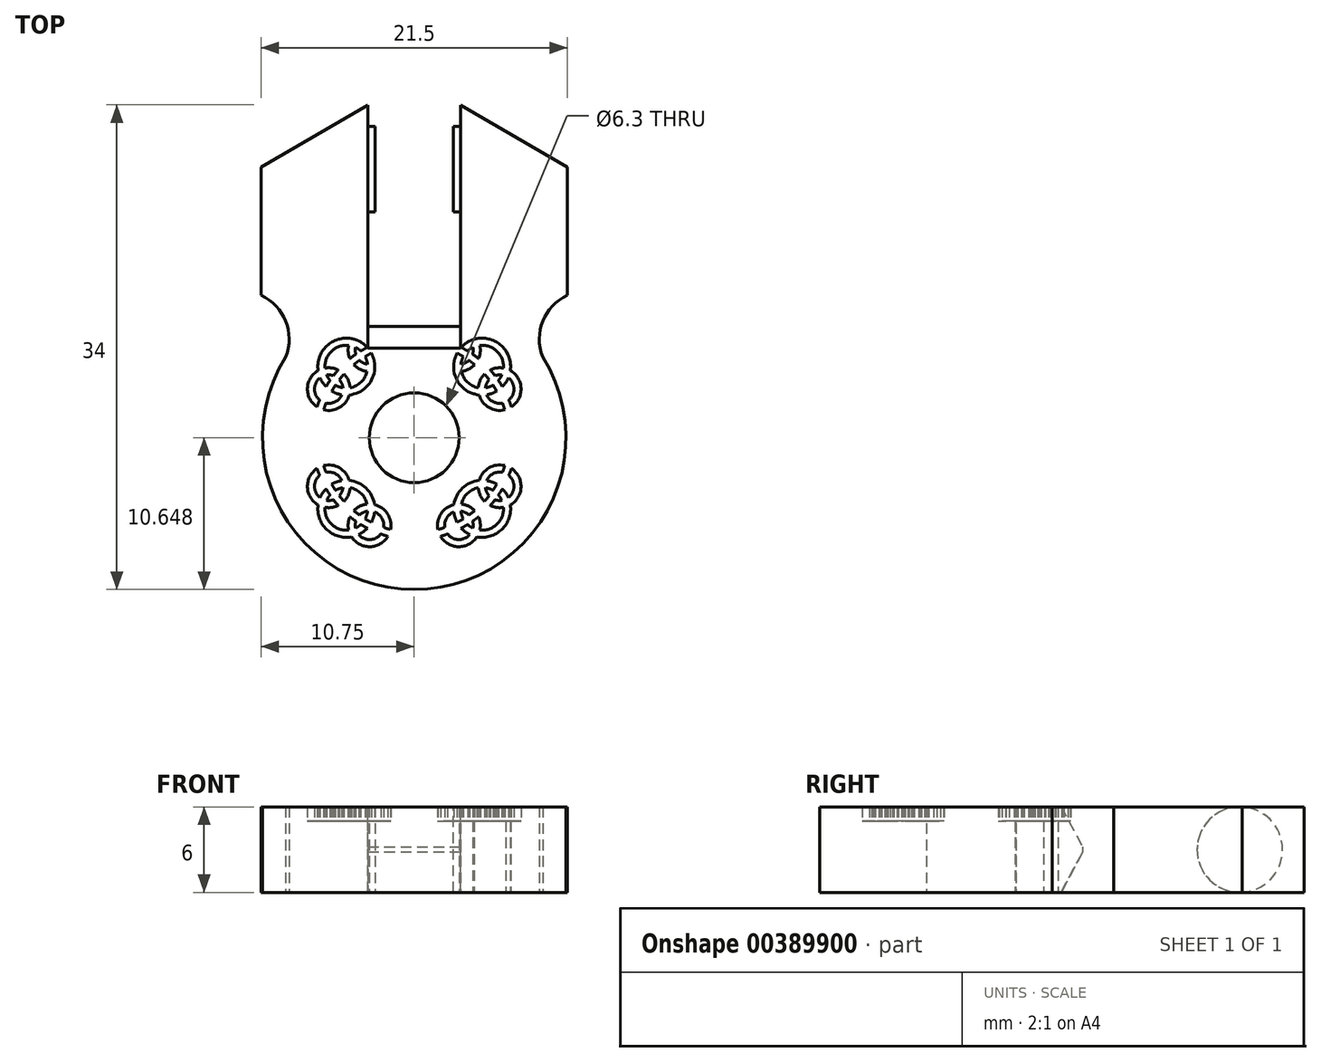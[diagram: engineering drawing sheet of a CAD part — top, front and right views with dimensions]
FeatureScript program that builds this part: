
annotation { "Feature Type Name" : "Feature", "Feature Type Description" : "" }
export const myFeature = defineFeature(function(context is Context, id is Id, definition is map)
    precondition{}
    {
        {
            var Q0;
            Q0=qCreatedBy(makeId("Top.planeOp"),FACE);
            var sketch = newSketch(context, id + "F0", { "sketchPlane" : qUnion([Q0])});
            skArc(sketch, "E0", {"start": v(29.04, 41) * mm, "mid": v(32.3, 20.22) * mm, "end": v(35.54, 41) * mm});
            skCircle(sketch, "E1", {"center": v(32.3, 30.87) * mm, "radius": 3.15 * mm});
            skLineSegment(sketch, "E2", {"start": v(35.54, 38.97) * mm, "end": v(35.54, 54.22) * mm});
            skLineSegment(sketch, "E3", {"start": v(43.04, 49.87) * mm, "end": v(35.54, 54.22) * mm});
            skLineSegment(sketch, "E4", {"start": v(43.04, 49.87) * mm, "end": v(43.04, 40.87) * mm});
            skLineSegment(sketch, "E5.MirrorCS", {"start": v(29.04, 38.97) * mm, "end": v(29.04, 54.22) * mm});
            skLineSegment(sketch, "E6.MirrorCS", {"start": v(21.54, 49.87) * mm, "end": v(29.04, 54.22) * mm});
            skLineSegment(sketch, "E7.MirrorCS", {"start": v(21.54, 49.87) * mm, "end": v(21.54, 40.87) * mm});
            skArc(sketch, "E8", {"start": v(43.04, 40.87) * mm, "mid": v(41.31, 39.04) * mm, "end": v(41.3, 36.53) * mm});
            skArc(sketch, "E9.MirrorCS", {"start": v(21.54, 40.87) * mm, "mid": v(23.27, 39.04) * mm, "end": v(23.27, 36.53) * mm});
            skArc(sketch, "E10", {"start": v(35.59, 24.52) * mm, "mid": v(35.87, 24.27) * mm, "end": v(36.2, 24.08) * mm});
            skArc(sketch, "E11", {"start": v(37.82, 27.17) * mm, "mid": v(37.57, 27.3) * mm, "end": v(37.3, 27.36) * mm});
            skArc(sketch, "E12", {"start": v(34.14, 23.96) * mm, "mid": v(35.4, 23.22) * mm, "end": v(36.7, 23.92) * mm});
            skArc(sketch, "E13", {"start": v(34.64, 24.11) * mm, "mid": v(35.4, 23.72) * mm, "end": v(36.2, 24.08) * mm});
            skArc(sketch, "E14", {"start": v(38.65, 28.91) * mm, "mid": v(37.54, 28.76) * mm, "end": v(36.85, 27.87) * mm});
            skArc(sketch, "E15", {"start": v(38.48, 28.44) * mm, "mid": v(37.82, 28.34) * mm, "end": v(37.37, 27.86) * mm});
            skArc(sketch, "E16.0", {"start": v(35.59, 24.52) * mm, "mid": v(35.82, 24.65) * mm, "end": v(36.04, 24.78) * mm});
            skArc(sketch, "E17.0", {"start": v(35.3, 24.94) * mm, "mid": v(35.52, 25.05) * mm, "end": v(35.73, 25.18) * mm});
            skArc(sketch, "E18.trimOffspring", {"start": v(34.14, 23.96) * mm, "mid": v(34.39, 24.03) * mm, "end": v(34.64, 24.11) * mm});
            skArc(sketch, "E19.trimOffspring", {"start": v(33.96, 24.43) * mm, "mid": v(34.2, 24.5) * mm, "end": v(34.44, 24.57) * mm});
            skArc(sketch, "E20.trimOffspring", {"start": v(38.08, 27.6) * mm, "mid": v(37.74, 27.76) * mm, "end": v(37.37, 27.86) * mm});
            skArc(sketch, "E21.trimOffspring", {"start": v(38.93, 28.22) * mm, "mid": v(39.03, 28.47) * mm, "end": v(39.1, 28.71) * mm});
            skArc(sketch, "E22.trimOffspring", {"start": v(38.48, 28.44) * mm, "mid": v(38.57, 28.68) * mm, "end": v(38.65, 28.91) * mm});
            skArc(sketch, "E23.trimOffspring", {"start": v(38.2, 26.85) * mm, "mid": v(38.35, 27.07) * mm, "end": v(38.48, 27.29) * mm});
            skArc(sketch, "E24.trimOffspring", {"start": v(37.82, 27.17) * mm, "mid": v(37.95, 27.38) * mm, "end": v(38.08, 27.6) * mm});
            skArc(sketch, "E25.trimOffspring", {"start": v(37.96, 26.51) * mm, "mid": v(38.2, 26.46) * mm, "end": v(38.44, 26.47) * mm});
            skArc(sketch, "E26.trimOffspring", {"start": v(37.63, 26.11) * mm, "mid": v(38.08, 25.97) * mm, "end": v(38.56, 25.98) * mm});
            skArc(sketch, "E27.trimOffspring", {"start": v(36.53, 25.74) * mm, "mid": v(36.1, 26.06) * mm, "end": v(35.6, 26.21) * mm});
            skArc(sketch, "E28.trimOffspring", {"start": v(36.13, 25.44) * mm, "mid": v(35.87, 25.62) * mm, "end": v(35.57, 25.71) * mm});
            skArc(sketch, "E29.trimOffspring", {"start": v(36.04, 24.78) * mm, "mid": v(36.22, 24.64) * mm, "end": v(36.4, 24.53) * mm});
            skArc(sketch, "E30.trimOffspring", {"start": v(37.63, 26.11) * mm, "mid": v(37.8, 26.3) * mm, "end": v(37.96, 26.51) * mm});
            skArc(sketch, "E31.trimOffspring", {"start": v(37.22, 26.4) * mm, "mid": v(37.39, 26.6) * mm, "end": v(37.54, 26.8) * mm});
            skArc(sketch, "E32.trimOffspring", {"start": v(36.13, 25.44) * mm, "mid": v(36.33, 25.59) * mm, "end": v(36.53, 25.74) * mm});
            skArc(sketch, "E33.trimOffspring", {"start": v(36.39, 25) * mm, "mid": v(36.6, 25.16) * mm, "end": v(36.8, 25.32) * mm});
            skArc(sketch, "E34.MirrorCS", {"start": v(37.63, 35.62) * mm, "mid": v(38.08, 35.76) * mm, "end": v(38.56, 35.75) * mm});
            skArc(sketch, "E35.MirrorCS", {"start": v(37.96, 35.22) * mm, "mid": v(38.2, 35.27) * mm, "end": v(38.44, 35.27) * mm});
            skArc(sketch, "E36.trimOffspring", {"start": v(39.04, 26.16) * mm, "mid": v(39.79, 27.42) * mm, "end": v(39.1, 28.71) * mm});
            skArc(sketch, "E37.trimOffspring", {"start": v(38.9, 26.67) * mm, "mid": v(39.29, 27.44) * mm, "end": v(38.93, 28.22) * mm});
            skArc(sketch, "E38.trimOffspring", {"start": v(38.44, 26.47) * mm, "mid": v(38.34, 26.67) * mm, "end": v(38.2, 26.85) * mm});
            skArc(sketch, "E39.trimOffspring", {"start": v(38.9, 26.67) * mm, "mid": v(38.72, 27) * mm, "end": v(38.48, 27.29) * mm});
            skArc(sketch, "E40.trimOffspring", {"start": v(36.8, 27.36) * mm, "mid": v(36.02, 26.97) * mm, "end": v(35.6, 26.21) * mm});
            skArc(sketch, "E41.trimOffspring", {"start": v(37.3, 27.36) * mm, "mid": v(37.37, 27.06) * mm, "end": v(37.54, 26.8) * mm});
            skArc(sketch, "E42.trimOffspring", {"start": v(36.8, 27.36) * mm, "mid": v(36.92, 26.84) * mm, "end": v(37.22, 26.4) * mm});
            skArc(sketch, "E43.trimOffspring", {"start": v(36.85, 27.87) * mm, "mid": v(35.68, 27.33) * mm, "end": v(35.08, 26.18) * mm});
            skArc(sketch, "E44.trimOffspring", {"start": v(35.57, 25.71) * mm, "mid": v(35.63, 25.44) * mm, "end": v(35.73, 25.18) * mm});
            skArc(sketch, "E45.trimOffspring", {"start": v(35.07, 25.66) * mm, "mid": v(35.15, 25.29) * mm, "end": v(35.3, 24.94) * mm});
            skArc(sketch, "E46.trimOffspring", {"start": v(35.07, 25.66) * mm, "mid": v(34.57, 25.23) * mm, "end": v(34.44, 24.57) * mm});
            skArc(sketch, "E47.trimOffspring", {"start": v(35.08, 26.18) * mm, "mid": v(34.17, 25.53) * mm, "end": v(33.96, 24.43) * mm});
            skArc(sketch, "E48.trimOffspring", {"start": v(36.4, 24.53) * mm, "mid": v(36.43, 24.77) * mm, "end": v(36.39, 25) * mm});
            skArc(sketch, "E49.trimOffspring", {"start": v(36.9, 24.4) * mm, "mid": v(36.92, 24.86) * mm, "end": v(36.8, 25.32) * mm});
            skArc(sketch, "E50.trimOffspring", {"start": v(36.9, 24.4) * mm, "mid": v(38.1, 24.8) * mm, "end": v(38.56, 25.98) * mm});
            skArc(sketch, "E51.trimOffspring", {"start": v(36.7, 23.92) * mm, "mid": v(38.44, 24.44) * mm, "end": v(39.04, 26.16) * mm});
            skArc(sketch, "E52.MirrorCS", {"start": v(38.48, 33.3) * mm, "mid": v(38.57, 33.06) * mm, "end": v(38.65, 32.82) * mm});
            skArc(sketch, "E53.MirrorCS", {"start": v(38.93, 33.51) * mm, "mid": v(39.03, 33.27) * mm, "end": v(39.1, 33.02) * mm});
            skArc(sketch, "E54.MirrorCS", {"start": v(38.9, 35.07) * mm, "mid": v(39.29, 34.3) * mm, "end": v(38.93, 33.51) * mm});
            skArc(sketch, "E55.MirrorCS", {"start": v(38.9, 35.07) * mm, "mid": v(38.72, 34.74) * mm, "end": v(38.48, 34.45) * mm});
            skArc(sketch, "E56.MirrorCS", {"start": v(38.2, 34.89) * mm, "mid": v(38.35, 34.67) * mm, "end": v(38.48, 34.45) * mm});
            skArc(sketch, "E57.MirrorCS", {"start": v(37.82, 34.56) * mm, "mid": v(37.95, 34.35) * mm, "end": v(38.08, 34.14) * mm});
            skArc(sketch, "E58.MirrorCS", {"start": v(36.85, 33.87) * mm, "mid": v(35.68, 34.4) * mm, "end": v(35.08, 35.55) * mm});
            skArc(sketch, "E59.MirrorCS", {"start": v(36.7, 37.82) * mm, "mid": v(38.44, 37.3) * mm, "end": v(39.04, 35.58) * mm});
            skArc(sketch, "E60.MirrorCS", {"start": v(36.9, 37.35) * mm, "mid": v(38.1, 36.94) * mm, "end": v(38.56, 35.75) * mm});
            skArc(sketch, "E61.MirrorCS", {"start": v(36.8, 34.38) * mm, "mid": v(36.02, 34.77) * mm, "end": v(35.6, 35.52) * mm});
            skArc(sketch, "E62.MirrorCS", {"start": v(39.04, 35.58) * mm, "mid": v(39.79, 34.32) * mm, "end": v(39.1, 33.02) * mm});
            skArc(sketch, "E63.MirrorCS", {"start": v(38.65, 32.82) * mm, "mid": v(37.54, 32.98) * mm, "end": v(36.85, 33.87) * mm});
            skArc(sketch, "E64.MirrorCS", {"start": v(38.48, 33.3) * mm, "mid": v(37.82, 33.4) * mm, "end": v(37.37, 33.88) * mm});
            skArc(sketch, "E65.MirrorCS", {"start": v(38.08, 34.14) * mm, "mid": v(37.74, 33.97) * mm, "end": v(37.37, 33.88) * mm});
            skArc(sketch, "E66.MirrorCS", {"start": v(37.82, 34.56) * mm, "mid": v(37.57, 34.44) * mm, "end": v(37.3, 34.37) * mm});
            skArc(sketch, "E67.MirrorCS", {"start": v(37.3, 34.37) * mm, "mid": v(37.37, 34.68) * mm, "end": v(37.54, 34.94) * mm});
            skArc(sketch, "E68.MirrorCS", {"start": v(36.8, 34.38) * mm, "mid": v(36.92, 34.9) * mm, "end": v(37.22, 35.33) * mm});
            skArc(sketch, "E69.MirrorCS", {"start": v(37.22, 35.33) * mm, "mid": v(37.39, 35.14) * mm, "end": v(37.54, 34.94) * mm});
            skArc(sketch, "E70.MirrorCS", {"start": v(37.63, 35.62) * mm, "mid": v(37.8, 35.43) * mm, "end": v(37.96, 35.22) * mm});
            skArc(sketch, "E71.MirrorCS", {"start": v(35.07, 36.08) * mm, "mid": v(35.15, 36.45) * mm, "end": v(35.3, 36.8) * mm});
            skArc(sketch, "E72.MirrorCS", {"start": v(35.59, 37.21) * mm, "mid": v(35.87, 37.46) * mm, "end": v(36.2, 37.66) * mm});
            skArc(sketch, "E73.MirrorCS", {"start": v(35.59, 37.21) * mm, "mid": v(35.82, 37.09) * mm, "end": v(36.04, 36.96) * mm});
            skArc(sketch, "E74.MirrorCS", {"start": v(35.3, 36.8) * mm, "mid": v(35.52, 36.68) * mm, "end": v(35.73, 36.56) * mm});
            skArc(sketch, "E75.MirrorCS", {"start": v(36.9, 37.35) * mm, "mid": v(36.92, 36.87) * mm, "end": v(36.8, 36.41) * mm});
            skArc(sketch, "E76.MirrorCS", {"start": v(36.53, 36) * mm, "mid": v(36.1, 35.67) * mm, "end": v(35.6, 35.52) * mm});
            skArc(sketch, "E77.MirrorCS", {"start": v(36.13, 36.3) * mm, "mid": v(35.87, 36.12) * mm, "end": v(35.57, 36.02) * mm});
            skArc(sketch, "E78.MirrorCS", {"start": v(36.39, 36.73) * mm, "mid": v(36.6, 36.57) * mm, "end": v(36.8, 36.41) * mm});
            skArc(sketch, "E79.MirrorCS", {"start": v(36.13, 36.3) * mm, "mid": v(36.33, 36.15) * mm, "end": v(36.53, 36) * mm});
            skArc(sketch, "E80.MirrorCS", {"start": v(38.44, 35.27) * mm, "mid": v(38.34, 35.07) * mm, "end": v(38.2, 34.89) * mm});
            skArc(sketch, "E81.MirrorCS", {"start": v(36.4, 37.2) * mm, "mid": v(36.43, 36.97) * mm, "end": v(36.39, 36.73) * mm});
            skArc(sketch, "E82.MirrorCS", {"start": v(36.04, 36.96) * mm, "mid": v(36.22, 37.1) * mm, "end": v(36.4, 37.2) * mm});
            skArc(sketch, "E83.MirrorCS", {"start": v(35.57, 36.02) * mm, "mid": v(35.63, 36.3) * mm, "end": v(35.73, 36.56) * mm});
            skArc(sketch, "E84.MirrorCS", {"start": v(25.54, 26.16) * mm, "mid": v(24.8, 27.42) * mm, "end": v(25.47, 28.71) * mm});
            skArc(sketch, "E85.MirrorCS", {"start": v(25.93, 28.91) * mm, "mid": v(27.04, 28.76) * mm, "end": v(27.73, 27.87) * mm});
            skArc(sketch, "E86.MirrorCS", {"start": v(25.65, 28.22) * mm, "mid": v(25.56, 28.47) * mm, "end": v(25.47, 28.71) * mm});
            skArc(sketch, "E87.MirrorCS", {"start": v(26.1, 28.44) * mm, "mid": v(26.01, 28.68) * mm, "end": v(25.93, 28.91) * mm});
            skArc(sketch, "E88.MirrorCS", {"start": v(26.1, 28.44) * mm, "mid": v(26.76, 28.34) * mm, "end": v(27.2, 27.86) * mm});
            skArc(sketch, "E89.MirrorCS", {"start": v(25.68, 26.67) * mm, "mid": v(25.3, 27.44) * mm, "end": v(25.65, 28.22) * mm});
            skArc(sketch, "E90.MirrorCS", {"start": v(27.89, 23.92) * mm, "mid": v(26.14, 24.44) * mm, "end": v(25.54, 26.16) * mm});
            skArc(sketch, "E91.MirrorCS", {"start": v(27.69, 24.4) * mm, "mid": v(26.48, 24.8) * mm, "end": v(26.02, 25.98) * mm});
            skArc(sketch, "E92.MirrorCS", {"start": v(25.68, 26.67) * mm, "mid": v(25.86, 27) * mm, "end": v(26.1, 27.29) * mm});
            skArc(sketch, "E93.MirrorCS", {"start": v(26.76, 27.17) * mm, "mid": v(27.01, 27.3) * mm, "end": v(27.29, 27.36) * mm});
            skArc(sketch, "E94.MirrorCS", {"start": v(26.5, 27.6) * mm, "mid": v(26.84, 27.76) * mm, "end": v(27.2, 27.86) * mm});
            skArc(sketch, "E95.MirrorCS", {"start": v(26.76, 27.17) * mm, "mid": v(26.63, 27.38) * mm, "end": v(26.5, 27.6) * mm});
            skArc(sketch, "E96.MirrorCS", {"start": v(28.05, 25.74) * mm, "mid": v(28.48, 26.06) * mm, "end": v(28.98, 26.21) * mm});
            skArc(sketch, "E97.MirrorCS", {"start": v(28.45, 25.44) * mm, "mid": v(28.7, 25.62) * mm, "end": v(29.01, 25.71) * mm});
            skArc(sketch, "E98.MirrorCS", {"start": v(29.01, 25.71) * mm, "mid": v(28.95, 25.44) * mm, "end": v(28.85, 25.18) * mm});
            skArc(sketch, "E99.MirrorCS", {"start": v(29.5, 25.66) * mm, "mid": v(29.43, 25.29) * mm, "end": v(29.28, 24.94) * mm});
            skArc(sketch, "E100.MirrorCS", {"start": v(29.5, 25.66) * mm, "mid": v(30.02, 25.23) * mm, "end": v(30.14, 24.57) * mm});
            skArc(sketch, "E101.MirrorCS", {"start": v(29.5, 26.18) * mm, "mid": v(30.41, 25.53) * mm, "end": v(30.62, 24.43) * mm});
            skArc(sketch, "E102.MirrorCS", {"start": v(30.62, 24.43) * mm, "mid": v(30.38, 24.5) * mm, "end": v(30.14, 24.57) * mm});
            skArc(sketch, "E103.MirrorCS", {"start": v(30.44, 23.96) * mm, "mid": v(30.2, 24.03) * mm, "end": v(29.94, 24.11) * mm});
            skArc(sketch, "E104.MirrorCS", {"start": v(30.44, 23.96) * mm, "mid": v(29.18, 23.22) * mm, "end": v(27.89, 23.92) * mm});
            skArc(sketch, "E105.MirrorCS", {"start": v(29.94, 24.11) * mm, "mid": v(29.17, 23.72) * mm, "end": v(28.39, 24.08) * mm});
            skArc(sketch, "E106.MirrorCS", {"start": v(29, 24.52) * mm, "mid": v(28.7, 24.27) * mm, "end": v(28.39, 24.08) * mm});
            skArc(sketch, "E107.MirrorCS", {"start": v(27.79, 27.36) * mm, "mid": v(28.56, 26.97) * mm, "end": v(28.98, 26.21) * mm});
            skArc(sketch, "E108.MirrorCS", {"start": v(27.73, 27.87) * mm, "mid": v(28.9, 27.33) * mm, "end": v(29.5, 26.18) * mm});
            skArc(sketch, "E109.MirrorCS", {"start": v(26.95, 26.11) * mm, "mid": v(26.5, 25.97) * mm, "end": v(26.02, 25.98) * mm});
            skArc(sketch, "E110.MirrorCS", {"start": v(26.62, 26.51) * mm, "mid": v(26.38, 26.46) * mm, "end": v(26.14, 26.47) * mm});
            skArc(sketch, "E111.MirrorCS", {"start": v(27.36, 26.4) * mm, "mid": v(27.2, 26.6) * mm, "end": v(27.04, 26.8) * mm});
            skArc(sketch, "E112.MirrorCS", {"start": v(28.2, 25) * mm, "mid": v(27.98, 25.16) * mm, "end": v(27.78, 25.32) * mm});
            skArc(sketch, "E113.MirrorCS", {"start": v(28.45, 25.44) * mm, "mid": v(28.25, 25.59) * mm, "end": v(28.05, 25.74) * mm});
            skArc(sketch, "E114.MirrorCS", {"start": v(29.28, 24.94) * mm, "mid": v(29.06, 25.05) * mm, "end": v(28.85, 25.18) * mm});
            skArc(sketch, "E115.MirrorCS", {"start": v(27.29, 27.36) * mm, "mid": v(27.2, 27.06) * mm, "end": v(27.04, 26.8) * mm});
            skArc(sketch, "E116.MirrorCS", {"start": v(27.79, 27.36) * mm, "mid": v(27.66, 26.84) * mm, "end": v(27.36, 26.4) * mm});
            skArc(sketch, "E117.MirrorCS", {"start": v(27.69, 24.4) * mm, "mid": v(27.66, 24.86) * mm, "end": v(27.78, 25.32) * mm});
            skArc(sketch, "E118.MirrorCS", {"start": v(28.17, 24.53) * mm, "mid": v(28.15, 24.77) * mm, "end": v(28.2, 25) * mm});
            skArc(sketch, "E119.MirrorCS", {"start": v(28.54, 24.78) * mm, "mid": v(28.36, 24.64) * mm, "end": v(28.17, 24.53) * mm});
            skArc(sketch, "E120.MirrorCS", {"start": v(29, 24.52) * mm, "mid": v(28.76, 24.65) * mm, "end": v(28.54, 24.78) * mm});
            skArc(sketch, "E121.MirrorCS", {"start": v(26.95, 26.11) * mm, "mid": v(26.78, 26.3) * mm, "end": v(26.62, 26.51) * mm});
            skArc(sketch, "E122.MirrorCS", {"start": v(26.14, 26.47) * mm, "mid": v(26.24, 26.67) * mm, "end": v(26.38, 26.85) * mm});
            skArc(sketch, "E123.MirrorCS", {"start": v(26.38, 26.85) * mm, "mid": v(26.23, 27.07) * mm, "end": v(26.1, 27.29) * mm});
            skArc(sketch, "E124.MirrorCS", {"start": v(25.65, 33.51) * mm, "mid": v(25.56, 33.27) * mm, "end": v(25.47, 33.02) * mm});
            skArc(sketch, "E125.MirrorCS", {"start": v(26.1, 33.3) * mm, "mid": v(26.01, 33.06) * mm, "end": v(25.93, 32.82) * mm});
            skArc(sketch, "E126.MirrorCS", {"start": v(26.1, 33.3) * mm, "mid": v(26.76, 33.4) * mm, "end": v(27.2, 33.88) * mm});
            skArc(sketch, "E127.MirrorCS", {"start": v(25.93, 32.82) * mm, "mid": v(27.04, 32.98) * mm, "end": v(27.73, 33.87) * mm});
            skArc(sketch, "E128.MirrorCS", {"start": v(25.54, 35.58) * mm, "mid": v(24.8, 34.32) * mm, "end": v(25.47, 33.02) * mm});
            skArc(sketch, "E129.MirrorCS", {"start": v(25.68, 35.07) * mm, "mid": v(25.3, 34.3) * mm, "end": v(25.65, 33.51) * mm});
            skArc(sketch, "E130.MirrorCS", {"start": v(25.68, 35.07) * mm, "mid": v(25.86, 34.74) * mm, "end": v(26.1, 34.45) * mm});
            skArc(sketch, "E131.MirrorCS", {"start": v(26.5, 34.14) * mm, "mid": v(26.84, 33.97) * mm, "end": v(27.2, 33.88) * mm});
            skArc(sketch, "E132.MirrorCS", {"start": v(26.76, 34.56) * mm, "mid": v(26.63, 34.35) * mm, "end": v(26.5, 34.14) * mm});
            skArc(sketch, "E133.MirrorCS", {"start": v(26.38, 34.89) * mm, "mid": v(26.23, 34.67) * mm, "end": v(26.1, 34.45) * mm});
            skArc(sketch, "E134.MirrorCS", {"start": v(26.14, 35.27) * mm, "mid": v(26.24, 35.07) * mm, "end": v(26.38, 34.89) * mm});
            skArc(sketch, "E135.MirrorCS", {"start": v(26.76, 34.56) * mm, "mid": v(27.01, 34.44) * mm, "end": v(27.29, 34.37) * mm});
            skArc(sketch, "E136.MirrorCS", {"start": v(27.29, 34.37) * mm, "mid": v(27.2, 34.68) * mm, "end": v(27.04, 34.94) * mm});
            skArc(sketch, "E137.MirrorCS", {"start": v(26.62, 35.22) * mm, "mid": v(26.38, 35.27) * mm, "end": v(26.14, 35.27) * mm});
            skArc(sketch, "E138.MirrorCS", {"start": v(26.95, 35.62) * mm, "mid": v(26.5, 35.76) * mm, "end": v(26.02, 35.75) * mm});
            skArc(sketch, "E139.MirrorCS", {"start": v(27.79, 34.38) * mm, "mid": v(27.66, 34.9) * mm, "end": v(27.36, 35.33) * mm});
            skArc(sketch, "E140.MirrorCS", {"start": v(26.95, 35.62) * mm, "mid": v(26.78, 35.43) * mm, "end": v(26.62, 35.22) * mm});
            skArc(sketch, "E141.MirrorCS", {"start": v(27.36, 35.33) * mm, "mid": v(27.2, 35.14) * mm, "end": v(27.04, 34.94) * mm});
            skArc(sketch, "E142.MirrorCS", {"start": v(27.89, 37.82) * mm, "mid": v(26.14, 37.3) * mm, "end": v(25.54, 35.58) * mm});
            skArc(sketch, "E143.MirrorCS", {"start": v(27.69, 37.35) * mm, "mid": v(26.48, 36.94) * mm, "end": v(26.02, 35.75) * mm});
            skArc(sketch, "E144.MirrorCS", {"start": v(27.79, 34.38) * mm, "mid": v(28.56, 34.77) * mm, "end": v(28.98, 35.52) * mm});
            skArc(sketch, "E145.MirrorCS", {"start": v(27.73, 33.87) * mm, "mid": v(28.9, 34.4) * mm, "end": v(29.5, 35.55) * mm});
            skArc(sketch, "E146.MirrorCS", {"start": v(28.05, 36) * mm, "mid": v(28.48, 35.67) * mm, "end": v(28.98, 35.52) * mm});
            skArc(sketch, "E147.MirrorCS", {"start": v(27.69, 37.35) * mm, "mid": v(27.66, 36.87) * mm, "end": v(27.78, 36.41) * mm});
            skArc(sketch, "E148.MirrorCS", {"start": v(28.2, 36.73) * mm, "mid": v(27.98, 36.57) * mm, "end": v(27.78, 36.41) * mm});
            skArc(sketch, "E149.MirrorCS", {"start": v(28.45, 36.3) * mm, "mid": v(28.25, 36.15) * mm, "end": v(28.05, 36) * mm});
            skArc(sketch, "E150.MirrorCS", {"start": v(28.45, 36.3) * mm, "mid": v(28.7, 36.12) * mm, "end": v(29.01, 36.02) * mm});
            skArc(sketch, "E151.MirrorCS", {"start": v(28.17, 37.2) * mm, "mid": v(28.15, 36.97) * mm, "end": v(28.2, 36.73) * mm});
            skArc(sketch, "E152.MirrorCS", {"start": v(28.54, 36.96) * mm, "mid": v(28.36, 37.1) * mm, "end": v(28.17, 37.2) * mm});
            skArc(sketch, "E153.MirrorCS", {"start": v(29.5, 36.08) * mm, "mid": v(29.43, 36.45) * mm, "end": v(29.28, 36.8) * mm});
            skArc(sketch, "E154.MirrorCS", {"start": v(29.01, 36.02) * mm, "mid": v(28.95, 36.3) * mm, "end": v(28.85, 36.56) * mm});
            skArc(sketch, "E155.MirrorCS", {"start": v(29.28, 36.8) * mm, "mid": v(29.06, 36.68) * mm, "end": v(28.85, 36.56) * mm});
            skArc(sketch, "E156.MirrorCS", {"start": v(29, 37.21) * mm, "mid": v(28.76, 37.09) * mm, "end": v(28.54, 36.96) * mm});
            skArc(sketch, "E157.MirrorCS", {"start": v(29, 37.21) * mm, "mid": v(28.7, 37.46) * mm, "end": v(28.39, 37.66) * mm});
            skArc(sketch, "E158", {"start": v(28.39, 37.66) * mm, "mid": v(28.14, 37.75) * mm, "end": v(27.89, 37.82) * mm});
            skArc(sketch, "E159", {"start": v(29.5, 35.55) * mm, "mid": v(29.52, 35.82) * mm, "end": v(29.5, 36.08) * mm});
            skArc(sketch, "E160", {"start": v(36.7, 37.82) * mm, "mid": v(36.44, 37.75) * mm, "end": v(36.2, 37.66) * mm});
            skArc(sketch, "E161", {"start": v(35.07, 36.08) * mm, "mid": v(35.06, 35.82) * mm, "end": v(35.08, 35.55) * mm});
            skLineSegment(sketch, "E162", {"start": v(29.04, 38.97) * mm, "end": v(29.04, 38.67) * mm});
            skLineSegment(sketch, "E163", {"start": v(29.04, 38.67) * mm, "end": v(35.54, 38.67) * mm});
            skLineSegment(sketch, "E164", {"start": v(35.54, 38.67) * mm, "end": v(35.54, 38.97) * mm});
            skSolve(sketch);
        }
        {
            var Q0;
            Q0=qSketchRegion(id+"F0",true);
            extrude(context, id + "F1", {"entities" : qUnion([Q0]), "depth" : 6 * mm});
        }
        {
            var Q0;
            Q0=qCreatedBy(makeId("Right.planeOp"),FACE);
            var sketch = newSketch(context, id + "F2", { "sketchPlane" : qUnion([Q0])});
            skCircle(sketch, "E165", {"center": v(49.72, 3) * mm, "radius": 3 * mm});
            skSolve(sketch);
        }
        {
            var Q0;
            Q0=qSketchRegion(id+"F2",true);
            extrude(context, id + "F3", {"entities" : qUnion([Q0]), "operationType" : NewBodyOperationType.ADD, "depth" : 36.6 * mm, "hasSecondDirection" : true, "secondDirectionOppositeDirection" : false, "secondDirectionDepth" : 27.9 * mm});
        }
        {
            var Q0;
            Q0=qCreatedBy(makeId("Top.planeOp"),FACE);
            var sketch = newSketch(context, id + "F4", { "sketchPlane" : qUnion([Q0])});
            skLineSegment(sketch, "E166", {"start": v(29.54, 49.5) * mm, "end": v(29.54, 54.14) * mm});
            skLineSegment(sketch, "E167", {"start": v(29.54, 54.14) * mm, "end": v(35.04, 54.14) * mm});
            skLineSegment(sketch, "E168", {"start": v(35.04, 54.14) * mm, "end": v(35.04, 45.95) * mm});
            skLineSegment(sketch, "E169", {"start": v(35.04, 45.95) * mm, "end": v(29.54, 45.95) * mm});
            skLineSegment(sketch, "E170", {"start": v(29.54, 45.95) * mm, "end": v(29.54, 49.5) * mm});
            skPoint(sketch, "E171.end.orphan", {"position": v(35.04, 50.08) * mm});
            skSolve(sketch);
        }
        {
            var Q0;
            Q0=qSketchRegion(id+"F4",true);
            extrude(context, id + "F5", {"entities" : qUnion([Q0]), "operationType" : NewBodyOperationType.REMOVE, "depth" : 19 * mm, "hasSecondDirection" : true, "secondDirectionOppositeDirection" : true, "secondDirectionDepth" : 25 * mm});
        }
        {
            var Q0;
            Q0=makeQuery(id+"F1.opExtrude","CAP_EDGE",EDGE,{"disambiguationData":[OSD([sQuery(id+"F0.wireOp",EDGE,"E163")])],"isStart":false});
            var Q1;
            Q1=makeQuery(id+"F1.opExtrude","CAP_EDGE",EDGE,{"disambiguationData":[OSD([sQuery(id+"F0.wireOp",EDGE,"E163")])],"isStart":true});
            chamfer(context, id + "F6", {"entities" : qUnion([Q0, Q1]), "chamferType" : ChamferType.TWO_OFFSETS, "width1" : 2.8 * mm, "oppositeDirection" : false, "width2" : 1.5 * mm, "tangentPropagation" : true});
        }
        {
            var Q0;
            Q0=qCreatedBy(makeId("Top.planeOp"),FACE);
            var sketch = newSketch(context, id + "F7", { "sketchPlane" : qUnion([Q0])});
            skEllipse(sketch, "E172", {"center": v(36.93, 25.9) * mm, "majorRadius": 5.54 * mm, "minorRadius": 2.45 * mm, "majorAxis": v(-0.62, -0.79)});
            skEllipse(sketch, "E173", {"center": v(27.5, 25.93) * mm, "majorRadius": 5.11 * mm, "minorRadius": 2.78 * mm, "majorAxis": v(0.78, -0.63)});
            skCircle(sketch, "E174", {"center": v(27.51, 35.85) * mm, "radius": 2.03 * mm});
            skCircle(sketch, "E175", {"center": v(37.05, 35.86) * mm, "radius": 2 * mm});
            skCircle(sketch, "E176", {"center": v(38.29, 34.29) * mm, "radius": 1.83 * mm});
            skCircle(sketch, "E177", {"center": v(26.18, 34.32) * mm, "radius": 2 * mm});
            skSolve(sketch);
        }
        {
            var Q0;
            Q0 = qSketchRegion(id + "F7", true);
            extrude(context, id + "F8", {"entities" : qUnion([Q0]), "operationType" : NewBodyOperationType.ADD, "depth" : 5 * mm});
        }
    });
